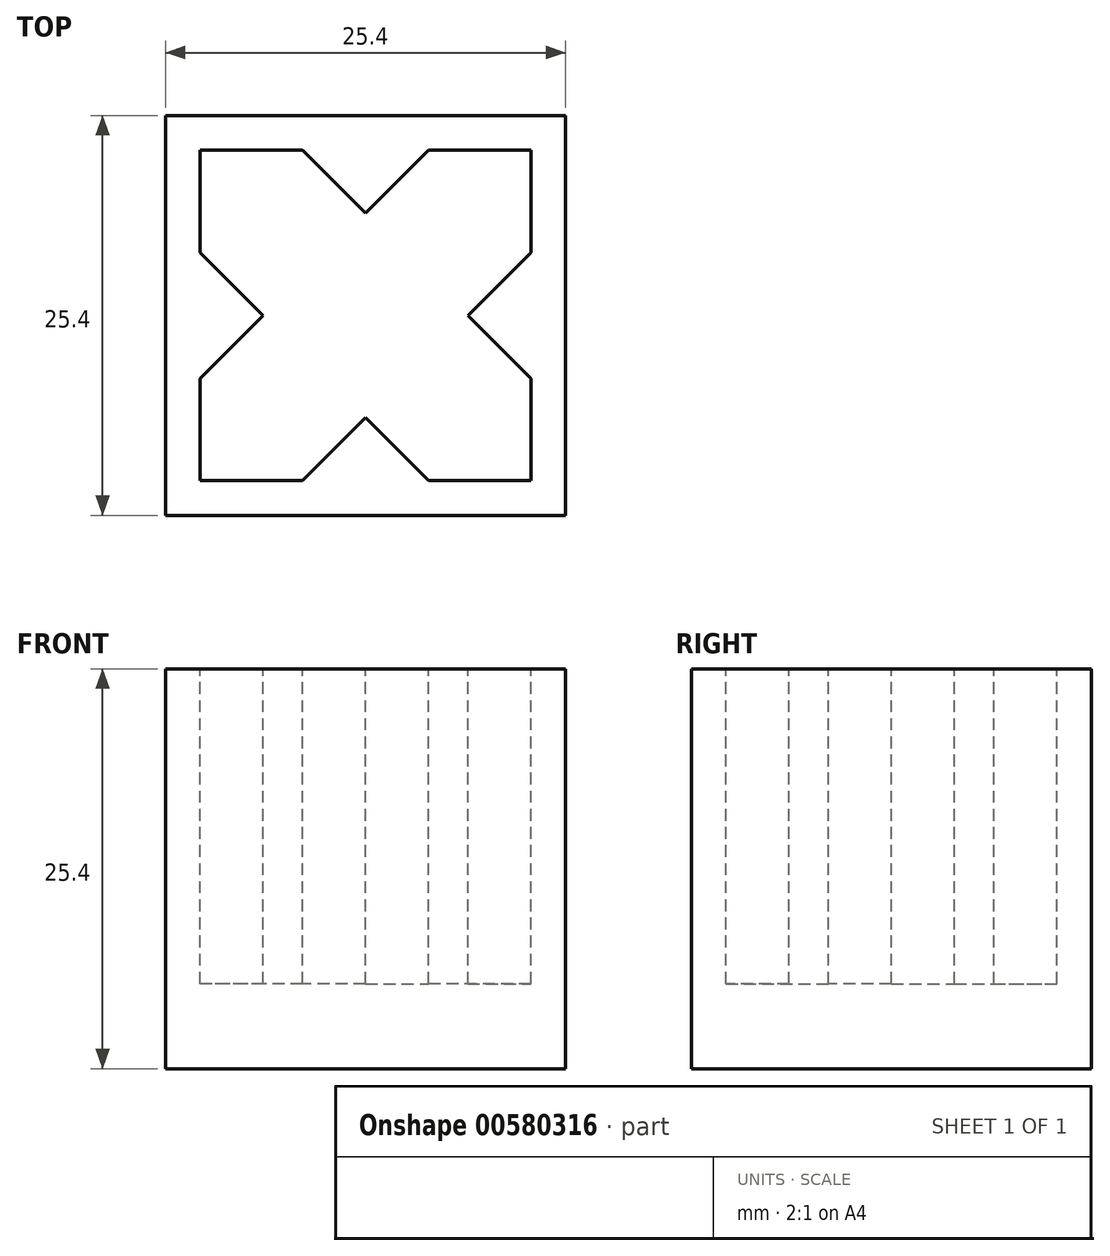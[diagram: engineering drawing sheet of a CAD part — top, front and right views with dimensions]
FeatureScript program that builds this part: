
annotation { "Feature Type Name" : "Feature", "Feature Type Description" : "" }
export const myFeature = defineFeature(function(context is Context, id is Id, definition is map)
    precondition{}
    {
        {
            var Q0;
            Q0=qCreatedBy(makeId("Top.planeOp"),FACE);
            var sketch = newSketch(context, id + "F0", { "sketchPlane" : qUnion([Q0])});
            skLineSegment(sketch, "E0.bottom", {"start": v(0, 0) * mm, "end": v(25.4, 0) * mm});
            skLineSegment(sketch, "E0.top", {"start": v(0, 25.4) * mm, "end": v(25.4, 25.4) * mm});
            skLineSegment(sketch, "E0.left", {"start": v(0, 0) * mm, "end": v(0, 25.4) * mm});
            skLineSegment(sketch, "E0.right", {"start": v(25.4, 0) * mm, "end": v(25.4, 25.4) * mm});
            skSolve(sketch);
        }
        {
            var Q0;
            Q0=qSketchRegion(id+"F0",true);
            extrude(context, id + "F1", {"entities" : qUnion([Q0]), "depth" : 25.4 * mm});
        }
        {
            var Q0;
            Q0=makeQuery(id+"F1.opExtrude","CAP_FACE",FACE,{"disambiguationData":[OSD([sQuery(id+"F0.wireOp",EDGE,"E0.bottom"),sQuery(id+"F0.wireOp",EDGE,"E0.top"),sQuery(id+"F0.wireOp",EDGE,"E0.left"),sQuery(id+"F0.wireOp",EDGE,"E0.right")])],"isStart":false});
            var sketch = newSketch(context, id + "F2", { "sketchPlane" : qUnion([Q0])});
            skLineSegment(sketch, "E1", {"start": v(0, 12.7) * mm, "end": v(25.4, 12.7) * mm});
            skLineSegment(sketch, "E2", {"start": v(12.7, 25.4) * mm, "end": v(12.7, 0) * mm});
            skLineSegment(sketch, "E3.bottom", {"start": v(23.2, 2.2) * mm, "end": v(2.2, 2.2) * mm});
            skLineSegment(sketch, "E3.top", {"start": v(23.2, 23.2) * mm, "end": v(2.2, 23.2) * mm});
            skLineSegment(sketch, "E3.left", {"start": v(23.2, 2.2) * mm, "end": v(23.2, 23.2) * mm});
            skLineSegment(sketch, "E3.right", {"start": v(2.2, 2.2) * mm, "end": v(2.2, 23.2) * mm});
            skPoint(sketch, "E3.middle", {"position": v(12.7, 12.7) * mm});
            skLineSegment(sketch, "E4", {"start": v(12.7, 6.2) * mm, "end": v(8.7, 2.2) * mm});
            skLineSegment(sketch, "E5", {"start": v(12.7, 6.2) * mm, "end": v(16.7, 2.2) * mm});
            skLineSegment(sketch, "E6.1.0", {"start": v(19.2, 12.7) * mm, "end": v(23.2, 16.7) * mm});
            skLineSegment(sketch, "E6.1.1", {"start": v(19.2, 12.7) * mm, "end": v(23.2, 8.7) * mm});
            skLineSegment(sketch, "E6.2.0", {"start": v(12.7, 19.2) * mm, "end": v(8.7, 23.2) * mm});
            skLineSegment(sketch, "E6.2.1", {"start": v(12.7, 19.2) * mm, "end": v(16.7, 23.2) * mm});
            skLineSegment(sketch, "E6.3.0", {"start": v(6.2, 12.7) * mm, "end": v(2.2, 8.7) * mm});
            skLineSegment(sketch, "E6.3.1", {"start": v(6.2, 12.7) * mm, "end": v(2.2, 16.7) * mm});
            skSolve(sketch);
        }
        {
            var Q0;
            {var subQ4=sQuery(id+"F2.wireOp",EDGE,"E5");Q0=makeQuery(id+"F2.imprint","IMPRINT",FACE,{"disambiguationData":[TD([[makeQuery(id+"F2.imprint","IMPRINT",EDGE,{"derivedFrom":subQ4}),1.0]])]});}
            var Q1;
            {var subQ3=sQuery(id+"F2.wireOp",EDGE,"E6.1.0");Q1=makeQuery(id+"F2.imprint","IMPRINT",FACE,{"disambiguationData":[TD([[makeQuery(id+"F2.imprint","IMPRINT",EDGE,{"derivedFrom":subQ3}),1.0]])]});}
            var Q2;
            {var subQ3=sQuery(id+"F2.wireOp",EDGE,"E4");Q2=makeQuery(id+"F2.imprint","IMPRINT",FACE,{"disambiguationData":[TD([[makeQuery(id+"F2.imprint","IMPRINT",EDGE,{"derivedFrom":subQ3}),-1.0]])]});}
            var Q3;
            {var subQ4=sQuery(id+"F2.wireOp",EDGE,"E6.2.0");Q3=makeQuery(id+"F2.imprint","IMPRINT",FACE,{"disambiguationData":[TD([[makeQuery(id+"F2.imprint","IMPRINT",EDGE,{"derivedFrom":subQ4}),1.0]])]});}
            extrude(context, id + "F3", {"entities" : qUnion([Q0, Q1, Q2, Q3]), "operationType" : NewBodyOperationType.REMOVE, "oppositeDirection" : true, "depth" : 20 * mm});
        }
    });
